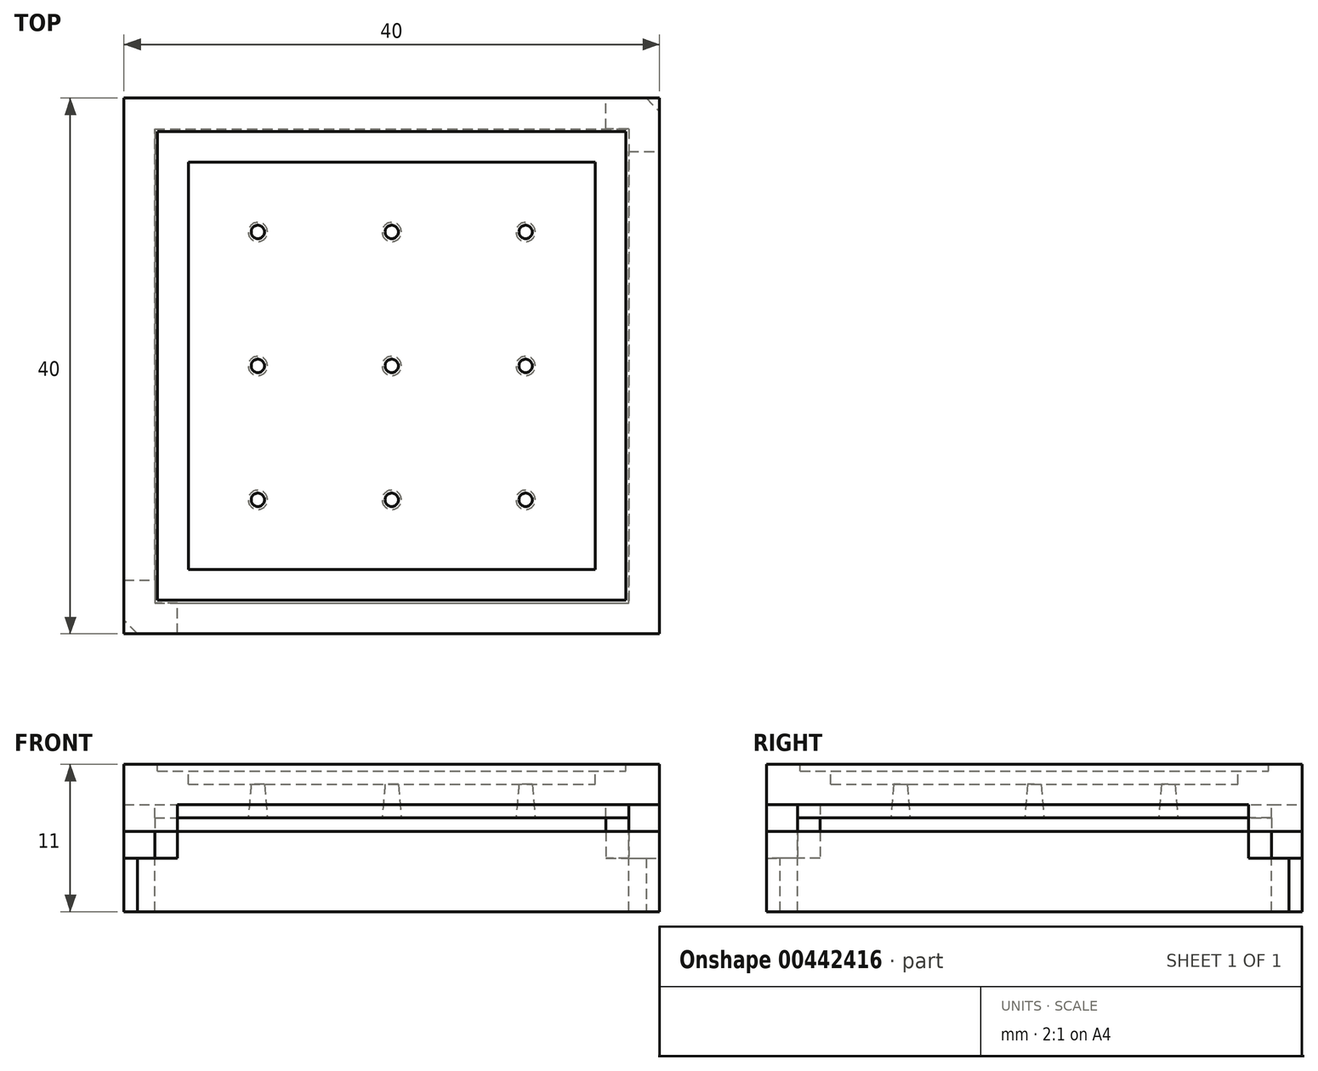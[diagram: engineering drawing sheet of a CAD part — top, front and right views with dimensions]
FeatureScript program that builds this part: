
annotation { "Feature Type Name" : "Feature", "Feature Type Description" : "" }
export const myFeature = defineFeature(function(context is Context, id is Id, definition is map)
    precondition{}
    {
        {
            var Q0;
            Q0=qCreatedBy(makeId("Top.planeOp"),FACE);
            var sketch = newSketch(context, id + "F0", { "sketchPlane" : qUnion([Q0])});
            skLineSegment(sketch, "E0.bottom", {"start": v(0, 0) * mm, "end": v(40, 0) * mm});
            skLineSegment(sketch, "E0.top", {"start": v(0, 40) * mm, "end": v(40, 40) * mm});
            skLineSegment(sketch, "E0.left", {"start": v(0, 0) * mm, "end": v(0, 40) * mm});
            skLineSegment(sketch, "E0.right", {"start": v(40, 0) * mm, "end": v(40, 40) * mm});
            skSolve(sketch);
        }
        {
            var Q0;
            Q0=qSketchRegion(id+"F0",true);
            extrude(context, id + "F1", {"entities" : qUnion([Q0]), "depth" : 6 * mm});
        }
        {
            var Q0;
            Q0=makeQuery(id+"F1.opExtrude","CAP_FACE",FACE,{"disambiguationData":[OSD([sQuery(id+"F0.wireOp",EDGE,"E0.bottom"),sQuery(id+"F0.wireOp",EDGE,"E0.top"),sQuery(id+"F0.wireOp",EDGE,"E0.left"),sQuery(id+"F0.wireOp",EDGE,"E0.right")])],"isStart":false});
            var sketch = newSketch(context, id + "F2", { "sketchPlane" : qUnion([Q0])});
            skLineSegment(sketch, "E1.bottom", {"start": v(2.3, 2.3) * mm, "end": v(37.7, 2.3) * mm});
            skLineSegment(sketch, "E1.top", {"start": v(2.3, 37.7) * mm, "end": v(37.7, 37.7) * mm});
            skLineSegment(sketch, "E1.left", {"start": v(2.3, 2.3) * mm, "end": v(2.3, 37.7) * mm});
            skLineSegment(sketch, "E1.right", {"start": v(37.7, 2.3) * mm, "end": v(37.7, 37.7) * mm});
            skSolve(sketch);
        }
        {
            var Q0;
            Q0=makeQuery(id+"F1.opExtrude","CAP_FACE",FACE,{"disambiguationData":[OSD([sQuery(id+"F0.wireOp",EDGE,"E0.bottom"),sQuery(id+"F0.wireOp",EDGE,"E0.top"),sQuery(id+"F0.wireOp",EDGE,"E0.left"),sQuery(id+"F0.wireOp",EDGE,"E0.right")])],"isStart":false});
            cPlane(context, id + "F3", {"entities" : qUnion([Q0]), "cplaneType" : CPlaneType.OFFSET, "offset" : 5 * mm, "width" : 150 * mm, "height" : 150 * mm});
        }
        {
            var Q0;
            Q0=qCreatedBy(id+"F3.planeOp",FACE);
            var sketch = newSketch(context, id + "F4", { "sketchPlane" : qUnion([Q0])});
            skLineSegment(sketch, "E2.bottom", {"start": v(0, 0) * mm, "end": v(40, 0) * mm});
            skLineSegment(sketch, "E2.top", {"start": v(0, 40) * mm, "end": v(40, 40) * mm});
            skLineSegment(sketch, "E2.left", {"start": v(0, 0) * mm, "end": v(0, 40) * mm});
            skLineSegment(sketch, "E2.right", {"start": v(40, 0) * mm, "end": v(40, 40) * mm});
            skSolve(sketch);
        }
        {
            var Q0;
            Q0=qSketchRegion(id+"F4",true);
            extrude(context, id + "F5", {"entities" : qUnion([Q0]), "oppositeDirection" : true, "depth" : 3 * mm});
        }
        {
            var Q0;
            Q0=makeQuery(id+"F2.imprint","IMPRINT",FACE,{"disambiguationData":[TD([[makeQuery(id+"F2.imprint","IMPRINT",EDGE,{"derivedFrom":sQuery(id+"F2.wireOp",EDGE,"E1.bottom")}),1.0]])]});
            extrude(context, id + "F6", {"entities" : qUnion([Q0]), "operationType" : NewBodyOperationType.REMOVE, "oppositeDirection" : true, "depth" : 1 * mm});
        }
        {
            var Q0;
            Q0=makeQuery(id+"F6.boolean.opBoolean","COPY",FACE,{"derivedFrom":makeQuery(id+"F6.opExtrude","CAP_FACE",FACE,{"disambiguationData":[OSD([sQuery(id+"F2.wireOp",EDGE,"E1.bottom"),sQuery(id+"F2.wireOp",EDGE,"E1.top"),sQuery(id+"F2.wireOp",EDGE,"E1.left"),sQuery(id+"F2.wireOp",EDGE,"E1.right")])],"isStart":false})});
            extrude(context, id + "F7", {"entities" : qUnion([Q0]), "operationType" : NewBodyOperationType.REMOVE, "oppositeDirection" : true, "depth" : 3 * mm, "hasDraft" : true, "draftAngle" : 10 * degree, "draftPullDirection" : true});
        }
        {
            var Q0;
            Q0=qCreatedBy(id+"FNHtQi6ISW0JxXh_2.planeOp",FACE);
            var sketch = newSketch(context, id + "F8", { "sketchPlane" : qUnion([Q0])});
            skCircle(sketch, "E3", {"center": v(0, 3) * mm, "radius": 0.25 * mm});
            skSolve(sketch);
        }
        {
            var Q0;
            Q0=makeQuery(id+"F5.opExtrude","CAP_FACE",FACE,{"disambiguationData":[OSD([sQuery(id+"F4.wireOp",EDGE,"E2.bottom"),sQuery(id+"F4.wireOp",EDGE,"E2.top"),sQuery(id+"F4.wireOp",EDGE,"E2.left"),sQuery(id+"F4.wireOp",EDGE,"E2.right")])],"isStart":false});
            var sketch = newSketch(context, id + "F9", { "sketchPlane" : qUnion([Q0])});
            skLineSegment(sketch, "E4.bottom", {"start": v(2.3, -2.3) * mm, "end": v(37.7, -2.3) * mm});
            skLineSegment(sketch, "E4.top", {"start": v(2.3, -37.7) * mm, "end": v(37.7, -37.7) * mm});
            skLineSegment(sketch, "E4.left", {"start": v(2.3, -2.3) * mm, "end": v(2.3, -37.7) * mm});
            skLineSegment(sketch, "E4.right", {"start": v(37.7, -2.3) * mm, "end": v(37.7, -37.7) * mm});
            skSolve(sketch);
        }
        {
            var Q0;
            Q0=makeQuery(id+"F9.imprint","IMPRINT",FACE,{"disambiguationData":[TD([[makeQuery(id+"F9.imprint","IMPRINT",EDGE,{"derivedFrom":sQuery(id+"F9.wireOp",EDGE,"E4.bottom")}),-1.0]])]});
            extrude(context, id + "F10", {"entities" : qUnion([Q0]), "operationType" : NewBodyOperationType.ADD, "depth" : 1 * mm});
        }
        {
            var Q0;
            Q0=makeQuery(id+"F5.opExtrude","CAP_FACE",FACE,{"disambiguationData":[OSD([sQuery(id+"F4.wireOp",EDGE,"E2.bottom"),sQuery(id+"F4.wireOp",EDGE,"E2.top"),sQuery(id+"F4.wireOp",EDGE,"E2.left"),sQuery(id+"F4.wireOp",EDGE,"E2.right")])],"isStart":true});
            shell(context, id + "F11", {"entities" : qUnion([Q0]), "thickness" : 2.5 * mm});
        }
        {
            var Q0;
            Q0=makeQuery(id+"F11.opShell","OFFSET_FACE",FACE,{"disambiguationData":[OSD([sQuery(id+"F9.wireOp",EDGE,"E4.bottom"),sQuery(id+"F9.wireOp",EDGE,"E4.top"),sQuery(id+"F9.wireOp",EDGE,"E4.left"),sQuery(id+"F9.wireOp",EDGE,"E4.right")])]});
            var sketch = newSketch(context, id + "F12", { "sketchPlane" : qUnion([Q0])});
            skCircle(sketch, "E5", {"center": v(10, 30) * mm, "radius": 0.5 * mm});
            skCircle(sketch, "E6.1.0.0", {"center": v(20, 30) * mm, "radius": 0.5 * mm});
            skCircle(sketch, "E6.2.0.0", {"center": v(30, 30) * mm, "radius": 0.5 * mm});
            skLineSegment(sketch, "E6.direction1", {"start": v(10, 30) * mm, "end": v(20, 30) * mm, "construction": true});
            skCircle(sketch, "E7.0.1.0", {"center": v(10, 20) * mm, "radius": 0.5 * mm});
            skCircle(sketch, "E7.0.2.0", {"center": v(10, 10) * mm, "radius": 0.5 * mm});
            skCircle(sketch, "E7.1.1.0", {"center": v(20, 20) * mm, "radius": 0.5 * mm});
            skCircle(sketch, "E7.1.2.0", {"center": v(20, 10) * mm, "radius": 0.5 * mm});
            skCircle(sketch, "E7.2.1.0", {"center": v(30, 20) * mm, "radius": 0.5 * mm});
            skCircle(sketch, "E7.2.2.0", {"center": v(30, 10) * mm, "radius": 0.5 * mm});
            skLineSegment(sketch, "E7.direction2", {"start": v(10, 30) * mm, "end": v(10, 20) * mm, "construction": true});
            skSolve(sketch);
        }
        {
            var Q0;
            Q0=qSketchRegion(id+"F12",true);
            extrude(context, id + "F13", {"entities" : qUnion([Q0]), "operationType" : NewBodyOperationType.REMOVE, "endBound" : BoundingType.UP_TO_NEXT, "oppositeDirection" : true, "depth" : 25 * mm, "hasDraft" : true, "draftAngle" : 5 * degree});
        }
        {
            var Q0;
            Q0=makeQuery(id+"F1.opExtrude","SWEPT_EDGE",EDGE,{"disambiguationData":[OSD([sQuery(id+"F0.wireOp",EDGE,"E0.bottom"),sQuery(id+"F0.wireOp",EDGE,"E0.left")])]});
            var Q1;
            Q1=makeQuery(id+"F1.opExtrude","SWEPT_EDGE",EDGE,{"disambiguationData":[OSD([sQuery(id+"F0.wireOp",EDGE,"E0.top"),sQuery(id+"F0.wireOp",EDGE,"E0.right")])]});
            chamfer(context, id + "F14", {"entities" : qUnion([Q0, Q1]), "width" : 1 * mm});
        }
        {
            var Q0;
            Q0=makeQuery(id+"F1.opExtrude","CAP_FACE",FACE,{"disambiguationData":[OSD([sQuery(id+"F0.wireOp",EDGE,"E0.bottom"),sQuery(id+"F0.wireOp",EDGE,"E0.top"),sQuery(id+"F0.wireOp",EDGE,"E0.left"),sQuery(id+"F0.wireOp",EDGE,"E0.right")])],"isStart":false});
            var sketch = newSketch(context, id + "F15", { "sketchPlane" : qUnion([Q0])});
            skLineSegment(sketch, "E8.bottom", {"start": v(0, 4) * mm, "end": v(4, 4) * mm});
            skLineSegment(sketch, "E8.top", {"start": v(0, 0) * mm, "end": v(4, 0) * mm});
            skLineSegment(sketch, "E8.left", {"start": v(0, 4) * mm, "end": v(0, 0) * mm});
            skLineSegment(sketch, "E8.right", {"start": v(4, 4) * mm, "end": v(4, 0) * mm});
            skLineSegment(sketch, "E9.bottom", {"start": v(36, 40) * mm, "end": v(40, 40) * mm});
            skLineSegment(sketch, "E9.top", {"start": v(36, 36) * mm, "end": v(40, 36) * mm});
            skLineSegment(sketch, "E9.left", {"start": v(36, 40) * mm, "end": v(36, 36) * mm});
            skLineSegment(sketch, "E9.right", {"start": v(40, 40) * mm, "end": v(40, 36) * mm});
            skSolve(sketch);
        }
        {
            var Q0;
            Q0=makeQuery(id+"F5.opExtrude","CAP_FACE",FACE,{"disambiguationData":[OSD([sQuery(id+"F4.wireOp",EDGE,"E2.bottom"),sQuery(id+"F4.wireOp",EDGE,"E2.top"),sQuery(id+"F4.wireOp",EDGE,"E2.left"),sQuery(id+"F4.wireOp",EDGE,"E2.right")])],"isStart":false});
            var sketch = newSketch(context, id + "F16", { "sketchPlane" : qUnion([Q0])});
            skSolve(sketch);
        }
        {
            var Q0;
            Q0=makeQuery(id+"F16.imprint","IMPRINT",FACE,{"disambiguationData":[TD([[makeQuery(id+"F16.imprint","IMPRINT",EDGE,{"derivedFrom":makeQuery(id+"F5.opExtrude","CAP_EDGE",EDGE,{"disambiguationData":[OSD([sQuery(id+"F4.wireOp",EDGE,"E2.bottom")])],"isStart":false})}),-1.0]])]});
            var sketch = newSketch(context, id + "F17", { "sketchPlane" : qUnion([Q0])});
            skLineSegment(sketch, "E10.bottom", {"start": v(0, 0) * mm, "end": v(4, 0) * mm});
            skLineSegment(sketch, "E10.top", {"start": v(0, -4) * mm, "end": v(4, -4) * mm});
            skLineSegment(sketch, "E10.left", {"start": v(0, 0) * mm, "end": v(0, -4) * mm});
            skLineSegment(sketch, "E10.right", {"start": v(4, 0) * mm, "end": v(4, -4) * mm});
            skLineSegment(sketch, "E11.bottom", {"start": v(36, -36) * mm, "end": v(40, -36) * mm});
            skLineSegment(sketch, "E11.top", {"start": v(36, -40) * mm, "end": v(40, -40) * mm});
            skLineSegment(sketch, "E11.left", {"start": v(36, -36) * mm, "end": v(36, -40) * mm});
            skLineSegment(sketch, "E11.right", {"start": v(40, -36) * mm, "end": v(40, -40) * mm});
            skSolve(sketch);
        }
        {
            var Q0;
            Q0=qSketchRegion(id+"F17",true);
            extrude(context, id + "F18", {"entities" : qUnion([Q0]), "operationType" : NewBodyOperationType.ADD, "depth" : 2 * mm});
        }
        {
            var Q0;
            Q0=makeQuery(id+"F10.opExtrude","CAP_FACE",FACE,{"disambiguationData":[OSD([sQuery(id+"F9.wireOp",EDGE,"E4.bottom"),sQuery(id+"F9.wireOp",EDGE,"E4.top"),sQuery(id+"F9.wireOp",EDGE,"E4.left"),sQuery(id+"F9.wireOp",EDGE,"E4.right")])],"isStart":false});
            var sketch = newSketch(context, id + "F19", { "sketchPlane" : qUnion([Q0])});
            skLineSegment(sketch, "E12.bottom", {"start": v(2.3, -37.7) * mm, "end": v(37.7, -37.7) * mm});
            skLineSegment(sketch, "E12.top", {"start": v(2.3, -2.3) * mm, "end": v(37.7, -2.3) * mm});
            skLineSegment(sketch, "E12.left", {"start": v(2.3, -37.7) * mm, "end": v(2.3, -2.3) * mm});
            skLineSegment(sketch, "E12.right", {"start": v(37.7, -37.7) * mm, "end": v(37.7, -2.3) * mm});
            skSolve(sketch);
        }
        {
            var Q0;
            Q0=qSketchRegion(id+"F19",true);
            extrude(context, id + "F20", {"entities" : qUnion([Q0]), "operationType" : NewBodyOperationType.REMOVE, "depth" : 25 * mm});
        }
        {
            var Q0;
            Q0=qSketchRegion(id+"F15",true);
            extrude(context, id + "F21", {"entities" : qUnion([Q0]), "operationType" : NewBodyOperationType.REMOVE, "oppositeDirection" : true, "depth" : 2 * mm});
        }
    });
